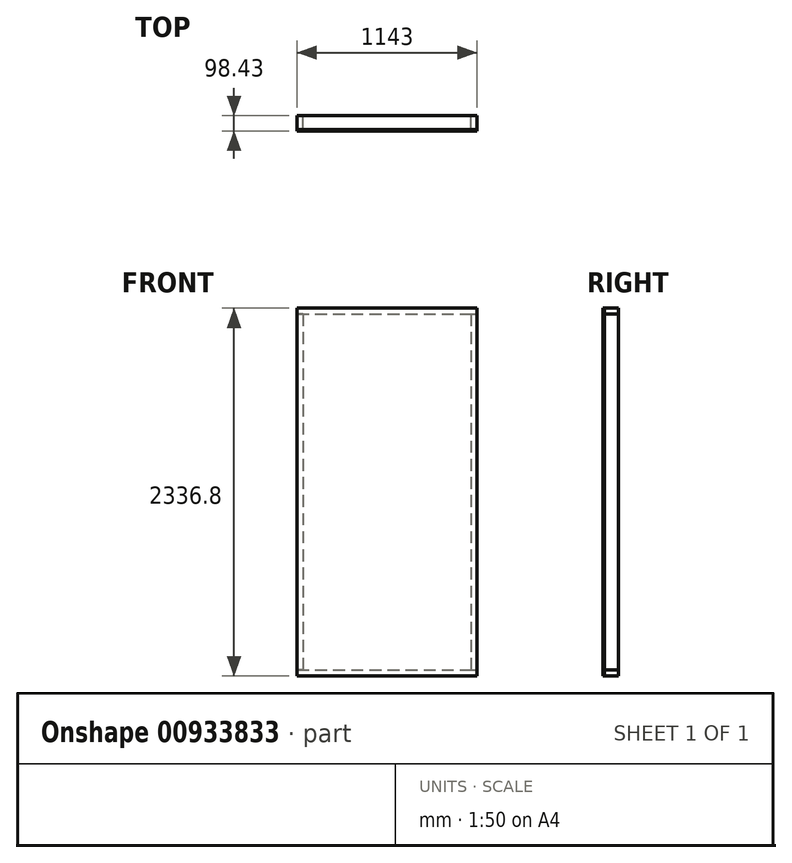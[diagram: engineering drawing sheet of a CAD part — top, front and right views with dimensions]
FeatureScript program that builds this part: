
annotation { "Feature Type Name" : "Feature", "Feature Type Description" : "" }
export const myFeature = defineFeature(function(context is Context, id is Id, definition is map)
    precondition{}
    {
        {
            var Q0;
            Q0=qCreatedBy(makeId("Front.planeOp"),FACE);
            var sketch = newSketch(context, id + "F0", { "sketchPlane" : qUnion([Q0])});
            skLineSegment(sketch, "E0.bottom", {"start": v(533.4, -1130.3) * mm, "end": v(-533.4, -1130.3) * mm, "construction": true});
            skLineSegment(sketch, "E0.top", {"start": v(533.4, 1130.3) * mm, "end": v(-533.4, 1130.3) * mm, "construction": true});
            skLineSegment(sketch, "E0.left", {"start": v(533.4, -1130.3) * mm, "end": v(533.4, 1130.3) * mm, "construction": true});
            skLineSegment(sketch, "E0.right", {"start": v(-533.4, -1130.3) * mm, "end": v(-533.4, 1130.3) * mm, "construction": true});
            skPoint(sketch, "E0.middle", {"position": v(0, 0) * mm});
            skLineSegment(sketch, "E1.bottom", {"start": v(-533.4, 1130.3) * mm, "end": v(-571.5, 1130.3) * mm});
            skLineSegment(sketch, "E1.top", {"start": v(-533.4, -1130.3) * mm, "end": v(-571.5, -1130.3) * mm});
            skLineSegment(sketch, "E1.left", {"start": v(-533.4, 1130.3) * mm, "end": v(-533.4, -1130.3) * mm});
            skLineSegment(sketch, "E1.right", {"start": v(-571.5, 1130.3) * mm, "end": v(-571.5, -1130.3) * mm});
            skLineSegment(sketch, "E2.bottom", {"start": v(533.4, 1130.3) * mm, "end": v(571.5, 1130.3) * mm});
            skLineSegment(sketch, "E2.top", {"start": v(533.4, -1130.3) * mm, "end": v(571.5, -1130.3) * mm});
            skLineSegment(sketch, "E2.left", {"start": v(533.4, 1130.3) * mm, "end": v(533.4, -1130.3) * mm});
            skLineSegment(sketch, "E2.right", {"start": v(571.5, 1130.3) * mm, "end": v(571.5, -1130.3) * mm});
            skLineSegment(sketch, "E3.bottom", {"start": v(-571.5, -1130.3) * mm, "end": v(571.5, -1130.3) * mm});
            skLineSegment(sketch, "E3.top", {"start": v(-571.5, -1168.4) * mm, "end": v(571.5, -1168.4) * mm});
            skLineSegment(sketch, "E3.left", {"start": v(-571.5, -1130.3) * mm, "end": v(-571.5, -1168.4) * mm});
            skLineSegment(sketch, "E3.right", {"start": v(571.5, -1130.3) * mm, "end": v(571.5, -1168.4) * mm});
            skLineSegment(sketch, "E4.bottom", {"start": v(-571.5, 1130.3) * mm, "end": v(571.5, 1130.3) * mm});
            skLineSegment(sketch, "E4.top", {"start": v(-571.5, 1168.4) * mm, "end": v(571.5, 1168.4) * mm});
            skLineSegment(sketch, "E4.left", {"start": v(-571.5, 1130.3) * mm, "end": v(-571.5, 1168.4) * mm});
            skLineSegment(sketch, "E4.right", {"start": v(571.5, 1130.3) * mm, "end": v(571.5, 1168.4) * mm});
            skLineSegment(sketch, "E5.bottom", {"start": v(-165.1, 1130.3) * mm, "end": v(-127, 1130.3) * mm});
            skLineSegment(sketch, "E5.top", {"start": v(-165.1, -1130.3) * mm, "end": v(-127, -1130.3) * mm});
            skLineSegment(sketch, "E5.left", {"start": v(-165.1, 1130.3) * mm, "end": v(-165.1, -1130.3) * mm});
            skLineSegment(sketch, "E5.right", {"start": v(-127, 1130.3) * mm, "end": v(-127, -1130.3) * mm});
            skLineSegment(sketch, "E6.bottom", {"start": v(241.3, 1130.3) * mm, "end": v(279.4, 1130.3) * mm});
            skLineSegment(sketch, "E6.top", {"start": v(241.3, -1130.3) * mm, "end": v(279.4, -1130.3) * mm});
            skLineSegment(sketch, "E6.left", {"start": v(241.3, 1130.3) * mm, "end": v(241.3, -1130.3) * mm});
            skLineSegment(sketch, "E6.right", {"start": v(279.4, 1130.3) * mm, "end": v(279.4, -1130.3) * mm});
            skSolve(sketch);
        }
        {
            var Q0;
            Q0=makeQuery(id+"F0.imprint","IMPRINT",FACE,{"disambiguationData":[TD([[makeQuery(id+"F0.imprint","IMPRINT",EDGE,{"derivedFrom":sQuery(id+"F0.wireOp",EDGE,"E4.top")}),-1.0]])]});
            var Q1;
            Q1=makeQuery(id+"F0.imprint","IMPRINT",FACE,{"disambiguationData":[TD([[makeQuery(id+"F0.imprint","IMPRINT",EDGE,{"derivedFrom":sQuery(id+"F0.wireOp",EDGE,"E3.top")}),1.0]])]});
            extrude(context, id + "F1", {"entities" : qUnion([Q0, Q1]), "endBound" : BoundingType.SYMMETRIC, "depth" : 88.9 * mm, "offsetDistance" : 25.4 * mm});
        }
        {
            var Q0;
            {var subQ0=sQuery(id+"F0.wireOp",EDGE,"E1.left");Q0=makeQuery(id+"F0.imprint","IMPRINT",FACE,{"disambiguationData":[TD([[makeQuery(id+"F0.imprint","IMPRINT",EDGE,{"derivedFrom":subQ0}),-1.0]])]});}
            var Q1;
            Q1=makeQuery(id+"F0.imprint","IMPRINT",FACE,{"disambiguationData":[TD([[makeQuery(id+"F0.imprint","IMPRINT",EDGE,{"derivedFrom":sQuery(id+"F0.wireOp",EDGE,"E5.bottom")}),-1.0]])]});
            var Q2;
            Q2=makeQuery(id+"F0.imprint","IMPRINT",FACE,{"disambiguationData":[TD([[makeQuery(id+"F0.imprint","IMPRINT",EDGE,{"derivedFrom":sQuery(id+"F0.wireOp",EDGE,"E6.bottom")}),-1.0]])]});
            var Q3;
            {var subQ0=sQuery(id+"F0.wireOp",EDGE,"E2.left");Q3=makeQuery(id+"F0.imprint","IMPRINT",FACE,{"disambiguationData":[TD([[makeQuery(id+"F0.imprint","IMPRINT",EDGE,{"derivedFrom":subQ0}),1.0]])]});}
            extrude(context, id + "F2", {"entities" : qUnion([Q0, Q1, Q2, Q3]), "endBound" : BoundingType.SYMMETRIC, "depth" : 88.9 * mm, "offsetDistance" : 25.4 * mm});
        }
        {
            var Q0;
            Q0=makeQuery(id+"F1.opExtrude","CAP_FACE",FACE,{"disambiguationData":[OSD([sQuery(id+"F0.wireOp",EDGE,"E4.bottom"),sQuery(id+"F0.wireOp",EDGE,"E4.top"),sQuery(id+"F0.wireOp",EDGE,"E4.left"),sQuery(id+"F0.wireOp",EDGE,"E4.right"),sQuery(id+"F0.wireOp",EDGE,"E5.bottom"),sQuery(id+"F0.wireOp",EDGE,"E6.bottom")])],"isStart":false});
            var sketch = newSketch(context, id + "F3", { "sketchPlane" : qUnion([Q0])});
            skLineSegment(sketch, "E7.bottom", {"start": v(-571.5, 1168.4) * mm, "end": v(571.5, 1168.4) * mm});
            skLineSegment(sketch, "E7.top", {"start": v(-571.5, -1168.4) * mm, "end": v(571.5, -1168.4) * mm});
            skLineSegment(sketch, "E7.left", {"start": v(-571.5, 1168.4) * mm, "end": v(-571.5, -1168.4) * mm});
            skLineSegment(sketch, "E7.right", {"start": v(571.5, 1168.4) * mm, "end": v(571.5, -1168.4) * mm});
            skSolve(sketch);
        }
        {
            var Q0;
            Q0 = qSketchRegion(id + "F3", true);
            extrude(context, id + "F4", {"entities" : qUnion([Q0]), "depth" : 9.52 * mm, "offsetDistance" : 25.4 * mm});
        }
    });
